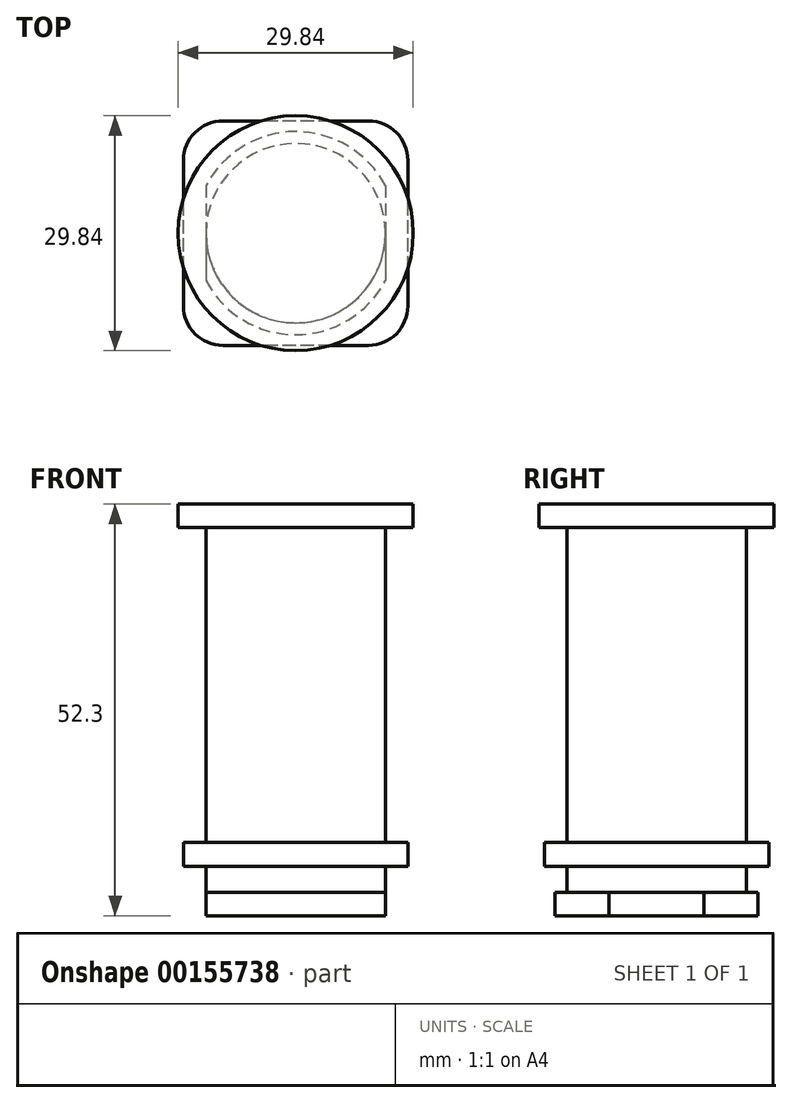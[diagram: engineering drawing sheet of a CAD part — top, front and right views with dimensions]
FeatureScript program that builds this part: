
annotation { "Feature Type Name" : "Feature", "Feature Type Description" : "" }
export const myFeature = defineFeature(function(context is Context, id is Id, definition is map)
    precondition{}
    {
        {
            var Q0;
            Q0=qCreatedBy(makeId("Top.planeOp"),FACE);
            var sketch = newSketch(context, id + "F0", { "sketchPlane" : qUnion([Q0])});
            skArc(sketch, "E0", {"start": v(-11.4, -6.04) * mm, "mid": v(0, -12.9) * mm, "end": v(11.4, -6.04) * mm});
            skLineSegment(sketch, "E1", {"start": v(-11.4, 6.04) * mm, "end": v(-11.4, -6.04) * mm});
            skLineSegment(sketch, "E2.MirrorCS", {"start": v(11.4, 6.04) * mm, "end": v(11.4, -6.04) * mm});
            skArc(sketch, "E3.trimOffspring", {"start": v(11.4, 6.04) * mm, "mid": v(0, 12.9) * mm, "end": v(-11.4, 6.04) * mm});
            skSolve(sketch);
        }
        {
            var Q0;
            Q0 = qSketchRegion(id + "F0", true);
            extrude(context, id + "F1", {"entities" : qUnion([Q0]), "depth" : 3 * mm});
        }
        {
            var Q0;
            Q0=makeQuery(id+"F1.opExtrude","CAP_FACE",FACE,{"disambiguationData":[OSD([sQuery(id+"F0.wireOp",EDGE,"E0"),sQuery(id+"F0.wireOp",EDGE,"E1"),sQuery(id+"F0.wireOp",EDGE,"E2.MirrorCS"),sQuery(id+"F0.wireOp",EDGE,"E3.trimOffspring")])],"isStart":false});
            var sketch = newSketch(context, id + "F2", { "sketchPlane" : qUnion([Q0])});
            skCircle(sketch, "E4", {"center": v(0, 0) * mm, "radius": 11.4 * mm});
            skSolve(sketch);
        }
        {
            var Q0;
            {var subQ0=sQuery(id+"F2.wireOp",EDGE,"E4");var subQ1=makeQuery(id+"F2.imprint","INTERSECT",VERTEX,{"derivedFrom":[makeQuery(id+"F1.opExtrude","CAP_EDGE",EDGE,{"disambiguationData":[OSD([sQuery(id+"F0.wireOp",EDGE,"E1")])],"isStart":false}),subQ0]});Q0=makeQuery(id+"F2.imprint","IMPRINT",FACE,{"disambiguationData":[TD([[makeQuery(id+"F2.imprint","IMPRINT",EDGE,{"disambiguationData":[TD([[subQ1,1.0]])],"derivedFrom":subQ0}),1.0]])]});}
            extrude(context, id + "F3", {"entities" : qUnion([Q0]), "operationType" : NewBodyOperationType.ADD, "depth" : 3.3 * mm});
        }
        {
            var Q0;
            Q0=makeQuery(id+"F3.opExtrude","CAP_FACE",FACE,{"disambiguationData":[OSD([sQuery(id+"F2.wireOp",EDGE,"E4")])],"isStart":false});
            var sketch = newSketch(context, id + "F4", { "sketchPlane" : qUnion([Q0])});
            skLineSegment(sketch, "E5.bottom", {"start": v(14.25, -14.25) * mm, "end": v(-14.25, -14.25) * mm});
            skLineSegment(sketch, "E5.top", {"start": v(14.25, 14.25) * mm, "end": v(-14.25, 14.25) * mm});
            skLineSegment(sketch, "E5.left", {"start": v(14.25, -14.25) * mm, "end": v(14.25, 14.25) * mm});
            skLineSegment(sketch, "E5.right", {"start": v(-14.25, -14.25) * mm, "end": v(-14.25, 14.25) * mm});
            skPoint(sketch, "E5.middle", {"position": v(0, 0) * mm});
            skSolve(sketch);
        }
        {
            var Q0;
            Q0=makeQuery(id+"F4.imprint","IMPRINT",FACE,{"disambiguationData":[TD([[makeQuery(id+"F4.imprint","IMPRINT",EDGE,{"derivedFrom":sQuery(id+"F4.wireOp",EDGE,"E5.bottom")}),-1.0]])]});
            var Q1;
            Q1=makeQuery(id+"F4.imprint","IMPRINT",FACE,{"disambiguationData":[TD([[makeQuery(id+"F4.imprint","IMPRINT",EDGE,{"derivedFrom":makeQuery(id+"F3.opExtrude","CAP_EDGE",EDGE,{"disambiguationData":[OSD([sQuery(id+"F2.wireOp",EDGE,"E4")])],"isStart":false})}),1.0]])]});
            extrude(context, id + "F5", {"entities" : qUnion([Q0, Q1]), "operationType" : NewBodyOperationType.ADD, "depth" : 3 * mm});
        }
        {
            var Q0;
            Q0=makeQuery(id+"F5.opExtrude","CAP_FACE",FACE,{"disambiguationData":[OSD([sQuery(id+"F4.wireOp",EDGE,"E5.bottom"),sQuery(id+"F4.wireOp",EDGE,"E5.top"),sQuery(id+"F4.wireOp",EDGE,"E5.left"),sQuery(id+"F4.wireOp",EDGE,"E5.right")])],"isStart":false});
            var sketch = newSketch(context, id + "F6", { "sketchPlane" : qUnion([Q0])});
            skCircle(sketch, "E6", {"center": v(0, 0) * mm, "radius": 11.4 * mm});
            skSolve(sketch);
        }
        {
            var Q0;
            Q0=makeQuery(id+"F6.imprint","IMPRINT",FACE,{"disambiguationData":[TD([[makeQuery(id+"F6.imprint","IMPRINT",EDGE,{"derivedFrom":sQuery(id+"F6.wireOp",EDGE,"E6")}),1.0]])]});
            extrude(context, id + "F7", {"entities" : qUnion([Q0]), "operationType" : NewBodyOperationType.ADD, "depth" : 40 * mm});
        }
        {
            var Q0;
            Q0=makeQuery(id+"F7.opExtrude","CAP_FACE",FACE,{"disambiguationData":[OSD([sQuery(id+"F6.wireOp",EDGE,"E6")])],"isStart":false});
            var sketch = newSketch(context, id + "F8", { "sketchPlane" : qUnion([Q0])});
            skCircle(sketch, "E7", {"center": v(0, 0) * mm, "radius": 14.92 * mm});
            skSolve(sketch);
        }
        {
            var Q0;
            Q0=makeQuery(id+"F8.imprint","IMPRINT",FACE,{"disambiguationData":[TD([[makeQuery(id+"F8.imprint","IMPRINT",EDGE,{"derivedFrom":sQuery(id+"F8.wireOp",EDGE,"E7")}),1.0]])]});
            var Q1;
            Q1=makeQuery(id+"F8.imprint","IMPRINT",FACE,{"disambiguationData":[TD([[makeQuery(id+"F8.imprint","IMPRINT",EDGE,{"derivedFrom":makeQuery(id+"F7.opExtrude","CAP_EDGE",EDGE,{"disambiguationData":[OSD([sQuery(id+"F6.wireOp",EDGE,"E6")])],"isStart":false})}),1.0]])]});
            extrude(context, id + "F9", {"entities" : qUnion([Q0, Q1]), "operationType" : NewBodyOperationType.ADD, "depth" : 3 * mm});
        }
        {
            var Q0;
            Q0=makeQuery(id+"F5.opExtrude","SWEPT_EDGE",EDGE,{"disambiguationData":[OSD([sQuery(id+"F4.wireOp",EDGE,"E5.top"),sQuery(id+"F4.wireOp",EDGE,"E5.left")])]});
            var Q1;
            Q1=makeQuery(id+"F5.opExtrude","SWEPT_EDGE",EDGE,{"disambiguationData":[OSD([sQuery(id+"F4.wireOp",EDGE,"E5.bottom"),sQuery(id+"F4.wireOp",EDGE,"E5.left")])]});
            var Q2;
            Q2=makeQuery(id+"F5.opExtrude","SWEPT_EDGE",EDGE,{"disambiguationData":[OSD([sQuery(id+"F4.wireOp",EDGE,"E5.top"),sQuery(id+"F4.wireOp",EDGE,"E5.right")])]});
            var Q3;
            Q3=makeQuery(id+"F5.opExtrude","SWEPT_EDGE",EDGE,{"disambiguationData":[OSD([sQuery(id+"F4.wireOp",EDGE,"E5.bottom"),sQuery(id+"F4.wireOp",EDGE,"E5.right")])]});
            var Q4;
            Q4=makeQuery(id+"F7.opExtrude","CAP_EDGE",EDGE,{"disambiguationData":[OSD([sQuery(id+"F6.wireOp",EDGE,"E6")])],"isStart":true});
            var Q5;
            Q5=makeQuery(id+"F7.opExtrude","CAP_EDGE",EDGE,{"disambiguationData":[OSD([sQuery(id+"F6.wireOp",EDGE,"E6")])],"isStart":false});
            fillet(context, id + "F10", {"entities" : qUnion([Q0, Q1, Q2, Q3, Q4, Q5]), "radius" : 5 * mm, "tangentPropagation" : true, "allowEdgeOverflow" : false});
        }
    });
